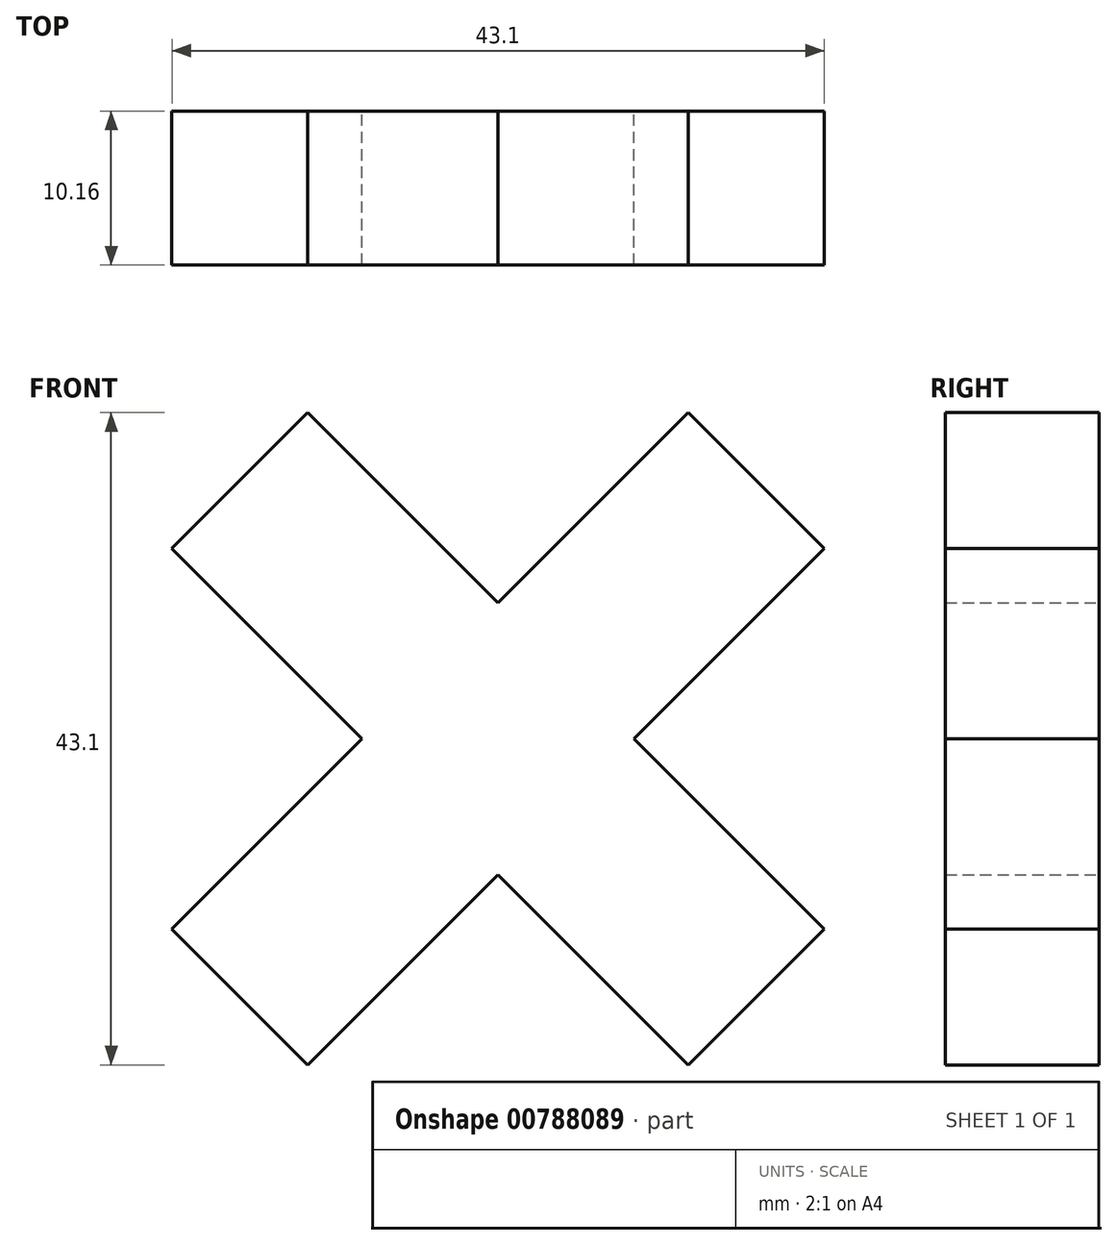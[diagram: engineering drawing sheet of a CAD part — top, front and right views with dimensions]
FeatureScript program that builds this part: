
annotation { "Feature Type Name" : "Feature", "Feature Type Description" : "" }
export const myFeature = defineFeature(function(context is Context, id is Id, definition is map)
    precondition{}
    {
        {
            var Q0;
            Q0=qCreatedBy(makeId("Front.planeOp"),FACE);
            var sketch = newSketch(context, id + "F0", { "sketchPlane" : qUnion([Q0])});
            skLineSegment(sketch, "E0", {"start": v(-54.1, 0) * mm, "end": v(-66.67, 12.57) * mm});
            skLineSegment(sketch, "E1", {"start": v(-66.67, 12.57) * mm, "end": v(-57.7, 21.55) * mm});
            skLineSegment(sketch, "E2", {"start": v(-57.7, 21.55) * mm, "end": v(-45.12, 8.98) * mm});
            skLineSegment(sketch, "E3", {"start": v(-45.12, 8.98) * mm, "end": v(-32.55, 21.55) * mm});
            skLineSegment(sketch, "E4", {"start": v(-32.55, 21.55) * mm, "end": v(-23.57, 12.57) * mm});
            skLineSegment(sketch, "E5", {"start": v(-23.57, 12.57) * mm, "end": v(-36.14, 0) * mm});
            skLineSegment(sketch, "E6", {"start": v(-36.14, 0) * mm, "end": v(-23.57, -12.57) * mm});
            skLineSegment(sketch, "E7", {"start": v(-23.57, -12.57) * mm, "end": v(-32.55, -21.55) * mm});
            skLineSegment(sketch, "E8", {"start": v(-32.55, -21.55) * mm, "end": v(-45.12, -8.98) * mm});
            skLineSegment(sketch, "E9", {"start": v(-45.12, -8.98) * mm, "end": v(-57.7, -21.55) * mm});
            skLineSegment(sketch, "E10", {"start": v(-57.7, -21.55) * mm, "end": v(-66.67, -12.57) * mm});
            skLineSegment(sketch, "E11", {"start": v(-66.67, -12.57) * mm, "end": v(-54.1, 0) * mm});
            skSolve(sketch);
        }
        {
            var Q0;
            Q0=makeQuery(id+"F0.imprint","IMPRINT",FACE,{"disambiguationData":[TD([[makeQuery(id+"F0.imprint","IMPRINT",EDGE,{"derivedFrom":sQuery(id+"F0.wireOp",EDGE,"E0")}),-1.0]])]});
            extrude(context, id + "F1", {"entities" : qUnion([Q0]), "depth" : 10.16 * mm, "offsetDistance" : 25.4 * mm});
        }
    });
